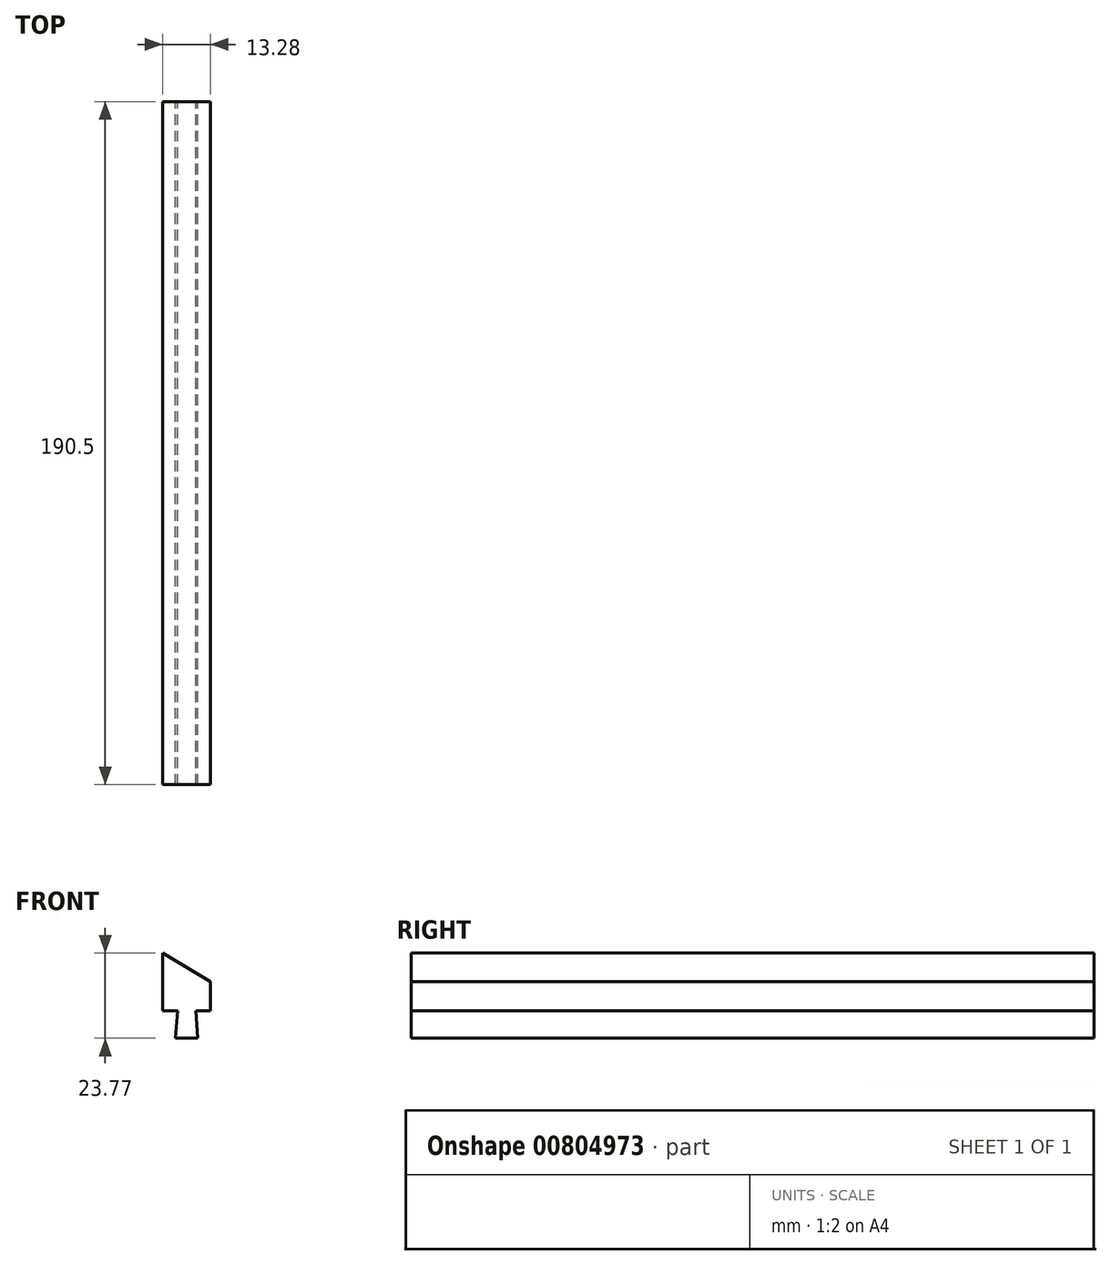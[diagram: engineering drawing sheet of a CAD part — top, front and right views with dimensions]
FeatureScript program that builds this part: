
annotation { "Feature Type Name" : "Feature", "Feature Type Description" : "" }
export const myFeature = defineFeature(function(context is Context, id is Id, definition is map)
    precondition{}
    {
        {
            var Q0;
            Q0=qCreatedBy(makeId("Front.planeOp"),FACE);
            var sketch = newSketch(context, id + "F0", { "sketchPlane" : qUnion([Q0])});
            skLineSegment(sketch, "E0", {"start": v(4.13, 0) * mm, "end": v(0, 0) * mm});
            skLineSegment(sketch, "E1", {"start": v(0, 0) * mm, "end": v(0, 16.15) * mm});
            skLineSegment(sketch, "E2", {"start": v(0, 16.15) * mm, "end": v(13.28, 8.13) * mm});
            skLineSegment(sketch, "E3", {"start": v(13.28, 8.13) * mm, "end": v(13.28, 0) * mm});
            skLineSegment(sketch, "E4", {"start": v(13.28, 0) * mm, "end": v(9.2, 0) * mm});
            skLineSegment(sketch, "E5", {"start": v(4.13, 0) * mm, "end": v(3.53, -7.62) * mm});
            skLineSegment(sketch, "E6", {"start": v(3.53, -7.62) * mm, "end": v(9.75, -7.62) * mm});
            skLineSegment(sketch, "E7", {"start": v(9.75, -7.62) * mm, "end": v(9.2, 0) * mm});
            skPoint(sketch, "E8.orphan", {"position": v(0, 0) * mm});
            skSolve(sketch);
        }
        {
            var Q0;
            Q0 = qSketchRegion(id + "F0", true);
            extrude(context, id + "F1", {"entities" : qUnion([Q0]), "depth" : 190.5 * mm, "offsetDistance" : 25.4 * mm});
        }
    });
